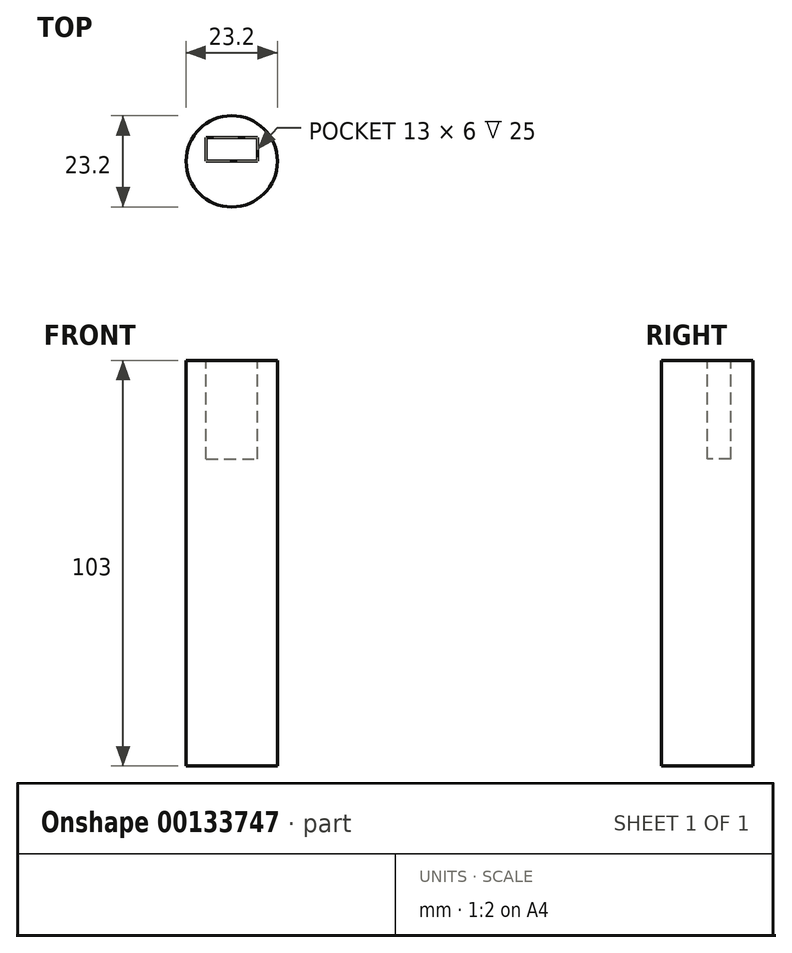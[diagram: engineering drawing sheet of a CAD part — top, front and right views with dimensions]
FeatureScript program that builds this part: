
annotation { "Feature Type Name" : "Feature", "Feature Type Description" : "" }
export const myFeature = defineFeature(function(context is Context, id is Id, definition is map)
    precondition{}
    {
        {
            var Q0;
            Q0=qCreatedBy(makeId("Top.planeOp"),FACE);
            var sketch = newSketch(context, id + "F0", { "sketchPlane" : qUnion([Q0])});
            skLineSegment(sketch, "E0.bottom", {"start": v(-6.3, 11.3) * mm, "end": v(6.3, 11.3) * mm, "construction": true});
            skLineSegment(sketch, "E0.top", {"start": v(-6.3, -11.3) * mm, "end": v(6.3, -11.3) * mm, "construction": true});
            skLineSegment(sketch, "E0.left", {"start": v(-11.3, 6.3) * mm, "end": v(-11.3, -6.3) * mm, "construction": true});
            skLineSegment(sketch, "E0.right", {"start": v(11.3, 6.3) * mm, "end": v(11.3, -6.3) * mm, "construction": true});
            skPoint(sketch, "E1", {"position": v(-11.3, 0) * mm});
            skPoint(sketch, "E2", {"position": v(0, 11.3) * mm});
            skPoint(sketch, "E3.visualSharp", {"position": v(-11.3, 11.3) * mm});
            skArc(sketch, "E3.filletArc", {"start": v(-6.3, 11.3) * mm, "mid": v(-9.84, 9.84) * mm, "end": v(-11.3, 6.3) * mm, "construction": true});
            skPoint(sketch, "E4.visualSharp", {"position": v(-11.3, -11.3) * mm});
            skArc(sketch, "E4.filletArc", {"start": v(-11.3, -6.3) * mm, "mid": v(-9.84, -9.84) * mm, "end": v(-6.3, -11.3) * mm, "construction": true});
            skPoint(sketch, "E5.visualSharp", {"position": v(11.3, -11.3) * mm});
            skArc(sketch, "E5.filletArc", {"start": v(6.3, -11.3) * mm, "mid": v(9.84, -9.84) * mm, "end": v(11.3, -6.3) * mm, "construction": true});
            skPoint(sketch, "E6.visualSharp", {"position": v(11.3, 11.3) * mm});
            skArc(sketch, "E6.filletArc", {"start": v(11.3, 6.3) * mm, "mid": v(9.84, 9.84) * mm, "end": v(6.3, 11.3) * mm, "construction": true});
            skCircle(sketch, "E7", {"center": v(0, 0) * mm, "radius": 11.6 * mm});
            skSolve(sketch);
        }
        {
            var Q0;
            Q0 = qSketchRegion(id + "F0", true);
            extrude(context, id + "F1", {"entities" : qUnion([Q0]), "depth" : 103 * mm});
        }
        {
            var Q0;
            Q0=makeQuery(id+"F1.opExtrude","CAP_FACE",FACE,{"disambiguationData":[OSD([sQuery(id+"F0.wireOp",EDGE,"E7")])],"isStart":false});
            var sketch = newSketch(context, id + "F2", { "sketchPlane" : qUnion([Q0])});
            skLineSegment(sketch, "E8.bottom", {"start": v(-6.5, 6) * mm, "end": v(6.5, 6) * mm});
            skLineSegment(sketch, "E8.top", {"start": v(-6.5, 0) * mm, "end": v(6.5, 0) * mm});
            skLineSegment(sketch, "E8.left", {"start": v(-6.5, 6) * mm, "end": v(-6.5, 0) * mm});
            skLineSegment(sketch, "E8.right", {"start": v(6.5, 6) * mm, "end": v(6.5, 0) * mm});
            skPoint(sketch, "E9", {"position": v(0, 6) * mm});
            skSolve(sketch);
        }
        {
            var Q0;
            Q0 = qSketchRegion(id + "F2", true);
            extrude(context, id + "F3", {"entities" : qUnion([Q0]), "operationType" : NewBodyOperationType.REMOVE, "oppositeDirection" : true, "depth" : 25 * mm});
        }
    });
